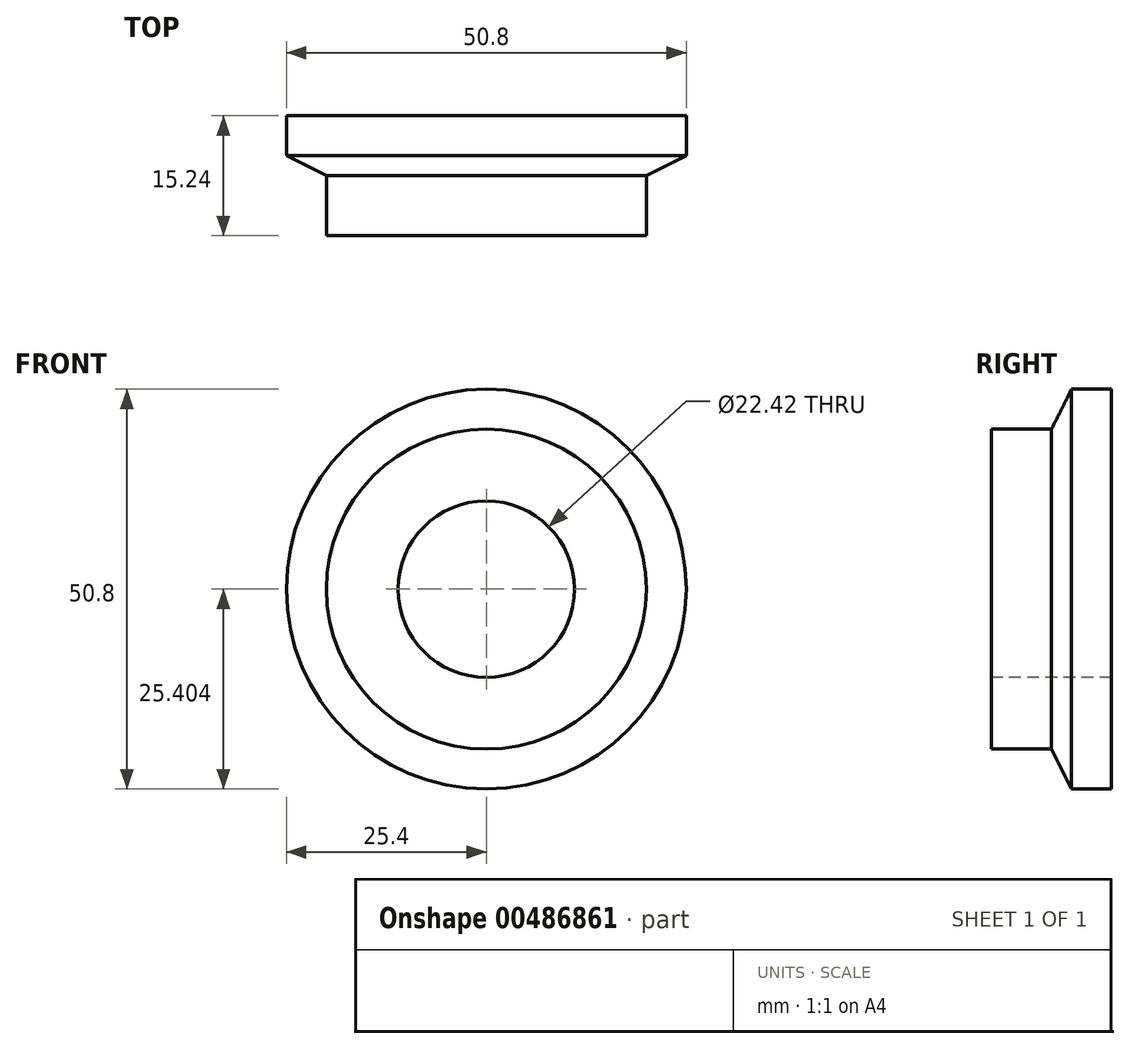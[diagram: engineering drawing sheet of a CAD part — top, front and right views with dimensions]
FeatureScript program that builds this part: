
annotation { "Feature Type Name" : "Feature", "Feature Type Description" : "" }
export const myFeature = defineFeature(function(context is Context, id is Id, definition is map)
    precondition{}
    {
        {
            var Q0;
            Q0=qCreatedBy(makeId("Right.planeOp"),FACE);
            var sketch = newSketch(context, id + "F0", { "sketchPlane" : qUnion([Q0])});
            skLineSegment(sketch, "E0", {"start": v(-7.62, 45.01) * mm, "end": v(0, 45.01) * mm});
            skLineSegment(sketch, "E1", {"start": v(0, 45.01) * mm, "end": v(2.54, 50.1) * mm});
            skLineSegment(sketch, "E2", {"start": v(2.54, 50.1) * mm, "end": v(7.62, 50.1) * mm});
            skLineSegment(sketch, "E3", {"start": v(7.62, 50.1) * mm, "end": v(7.62, 24.7) * mm});
            skLineSegment(sketch, "E4", {"start": v(7.62, 24.7) * mm, "end": v(-7.62, 24.7) * mm});
            skLineSegment(sketch, "E5", {"start": v(-7.62, 45.01) * mm, "end": v(-7.62, 24.7) * mm});
            skSolve(sketch);
        }
        {
            var Q0;
            Q0=makeQuery(id+"F0.imprint","IMPRINT",FACE,{"disambiguationData":[TD([[makeQuery(id+"F0.imprint","IMPRINT",EDGE,{"derivedFrom":sQuery(id+"F0.wireOp",EDGE,"E0")}),-1.0]])]});
            var Q1;
            Q1=sQuery(id+"F0.wireOp",EDGE,"E4");
            revolve(context, id + "F1", {"entities" : qUnion([Q0]), "axis" : qUnion([Q1]), "revolveType" : RevolveType.FULL});
        }
        {
            var Q0;
            Q0=makeQuery(id+"F1.opRevolve","SWEPT_FACE",FACE,{"disambiguationData":[OSD([sQuery(id+"F0.wireOp",EDGE,"E5")])]});
            var sketch = newSketch(context, id + "F2", { "sketchPlane" : qUnion([Q0])});
            skCircle(sketch, "E6", {"center": v(0, 24.7) * mm, "radius": 11.21 * mm});
            skSolve(sketch);
        }
        {
            var Q0;
            Q0=makeQuery(id+"F2.imprint","IMPRINT",FACE,{"disambiguationData":[TD([[makeQuery(id+"F2.imprint","IMPRINT",EDGE,{"derivedFrom":sQuery(id+"F2.wireOp",EDGE,"E6")}),1.0]])]});
            extrude(context, id + "F3", {"entities" : qUnion([Q0]), "operationType" : NewBodyOperationType.REMOVE, "endBound" : BoundingType.THROUGH_ALL, "oppositeDirection" : true, "depth" : 25.4 * mm, "offsetDistance" : 25.4 * mm});
        }
    });
